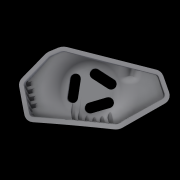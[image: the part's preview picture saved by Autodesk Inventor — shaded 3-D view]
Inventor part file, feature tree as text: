
AUTODESK INVENTOR PART (.ipt)
format: ipt  version: 2015 (Build 190159000, 159)  size: 1,354,752 bytes
history: native  units: mm
features: other x21, extrude x15, direct_edit x12, sketch x11, plane x9, fillet x7, surface_op x6, boolean_combine x3, move_body x3, imported_body x1, projected_geometry x1
ambient origin geometry x8: Origin, YZ Plane, XZ Plane, XY Plane, X Axis, Y Axis, Z Axis, Center Point
bodies: Solid1 (feature_tree), Solid2 (feature_tree), Solid3 (feature_tree), Solid4 (feature_tree)
feature tree (89):
  imported_body  "Base"
  extrude  "BaseFeature"  Depth=18.849556mm
  extrude  "SensorRailsFeature"  Depth=27.227136mm
  fillet  "SmallFilletsFeature"  Radius=24.783675mm
  fillet  "LargeFilletsFeature"  Radius=21.293017mm
  other  "SlopeProfileMiddlePlane"
  other  "SlopeProfileIntersect"
  other  "SlopeProfileIntersectFeature"
  other  "SlopeProfileSubtractFeature"
  other  "LeadsPlane"
  other  "Leads"
  extrude  "Leads1Feature"  Depth=5.0mm
  other  "FaceWireBase"
  other  "FaceWirePlane"
  other  "FaceWireProjected"
  extrude  "Extrusion6"  Depth=2.0mm TaperAngle=0.0deg
  sketch  "Sketch9"  dims[d8=25.481807mm d12=18.849556mm]
  surface_op  "Sculpt2"
  direct_edit  "Direct Edit9"
  sketch  "Sketch10"  dims[d13=21.642083mm d14=27.227136mm d15=24.783675mm d16=21.293017mm]
  surface_op  "Sculpt3"
  boolean_combine  "Combine2"
  direct_edit  "Direct Edit10"
  extrude  "Extrusion7"  Depth=25.5mm
  extrude  "Extrusion8"  [1 undecoded]
  direct_edit  "Direct Edit11"
  sketch  "Sketch11"  dims[d17=59.934mm d20=5.0mm]
  surface_op  "Sculpt4"
  boolean_combine  "Combine3"
  extrude  "Extrusion9"  Depth=4.0mm
  extrude  "Extrusion10"  Depth=66.357702mm
  direct_edit  "Direct Edit12"
  extrude  "Extrusion11"  Depth=0.5mm
  direct_edit  "Direct Edit13"
  surface_op  "Sculpt5"
  sketch  "Sketch13"  dims[d60=4.0mm d62=25.5mm]
  surface_op  "Sculpt6"
  boolean_combine  "Combine4"
  direct_edit  "Direct Edit14"
  direct_edit  "Direct Edit15"
  direct_edit  "Direct Edit16"
  direct_edit  "Direct Edit17"
  direct_edit  "Direct Edit19"
  surface_op  "Sculpt8"
  plane  "Work Plane14"
  plane  "Work Plane15"
  extrude  "Extrusion12"  Depth=0.5mm
  plane  "Work Plane16"
  extrude  "Extrusion14"  Depth=2.0mm
  fillet  "Fillet4"  Radius=8.0mm
  fillet  "Fillet5"  Radius=200.0mm
  fillet  "Fillet6"  Radius=10.0mm
  extrude  "Extrusion15"  Depth=2.0mm TaperAngle=0.0deg
  extrude  "Extrusion16"  TaperAngle=0.0deg  [1 undecoded]
  fillet  "Fillet8"  Radius=1.0mm
  extrude  "Extrusion17"  Depth=2.0mm TaperAngle=0.0deg
  direct_edit  "Direct Edit20"
  direct_edit  "Direct Edit21"
  extrude  "Extrusion19"  Depth=2.0mm TaperAngle=0.0deg
  fillet  "Fillet9"  Radius=2.5mm
  other  "SlopeProfilePlane"
  other  "SlopeProfileSubtract"
  plane  "Work Plane7"
  plane  "Work Plane8"
  plane  "Work Plane9"
  sketch  "Sketch12"  dims[d56=10.0mm d57=0.0mm d58=2.0mm d59=0.0mm]
  projected_geometry  "Projected Loop1"
  plane  "Work Plane10"
  plane  "Work Plane11"
  plane  "Work Plane13"
  sketch  "Sketch14"  dims[d63=6.0mm d64=-3.054326mm d68=-18.0mm]
  sketch  "Sketch16"  dims[d69=90.0deg d70=4.0mm]
  sketch  "Sketch17"  dims[d71=90.0deg d72=66.357702mm]
  sketch  "Sketch18"  dims[d76=0.5mm d77=0.5mm]
  sketch  "Sketch19"  dims[d78=0.5mm d79=0.5mm]
  sketch  "Sketch21"  dims[d80=0.5mm d81=0.5mm d82=8.0mm d83=0.0mm d84=200.0mm d85=10.0mm d96=2.0mm d97=0.0mm d98=0.0mm d99=0.0mm d100=-2.0mm d101=1.0mm d102=1.91mm d103=0.0mm d104=2.0mm d105=0.0mm d106=0.0mm d107=0.0mm d108=2.5mm d109=1.0mm d110=1.8mm d111=0.0mm d112=0.0mm d113=0.0mm d114=6.0mm d115=0.0mm d116=-0.2mm d117=2.5mm d118=0.0mm d119=-6.0mm d120=0.0mm d121=2.0mm d122=6.0mm d123=0.0mm d124=1.5mm d131=-2.0mm d132=2.0mm d133=0.0mm d134=13.0mm d135=6.0mm d136=20.0mm d138=0.8mm d139=1.8mm d140=2.5mm d141=2.5mm d142=20.0mm d143=0.0mm d144=5.2mm d145=2.5mm d146=10.0mm d147=0.0mm d148=5.0mm d149=0.693497mm d150=2.364391mm d151=6.521121mm d152=5.759587mm d153=30.242508mm d154=12.3mm d155=1.5mm d156=6.5mm d157=50.0mm d159=3.3mm d160=10.0mm d162=10.0mm d164=1.136417mm d166=2.636417mm d167=2.636417mm d168=2.5mm d169=3.3mm d170=0.0mm d190=1.5mm d197=2.636417mm d198=6.712536mm d199=2.636417mm d200=2.636417mm d201=2.636417mm d202=3.3mm d203=0.0mm d204=2.0mm]
  move_body  "Move3"
  other  "Delete7"
  move_body  "Move4"
  other  "Delete8"
  other  "Delete9"
  other  "Delete10"
  other  "Delete11"
  other  "Delete12"
  other  "Delete13"
  other  "Delete14"
  move_body  "Move5"
  other  "Delete16"
  other  "Delete17"
note: 2 required parameter values undecoded (feature->parameter linkage not recoverable at this tier; creation-order binding heuristic only, values carry confidence <= 0.55)
